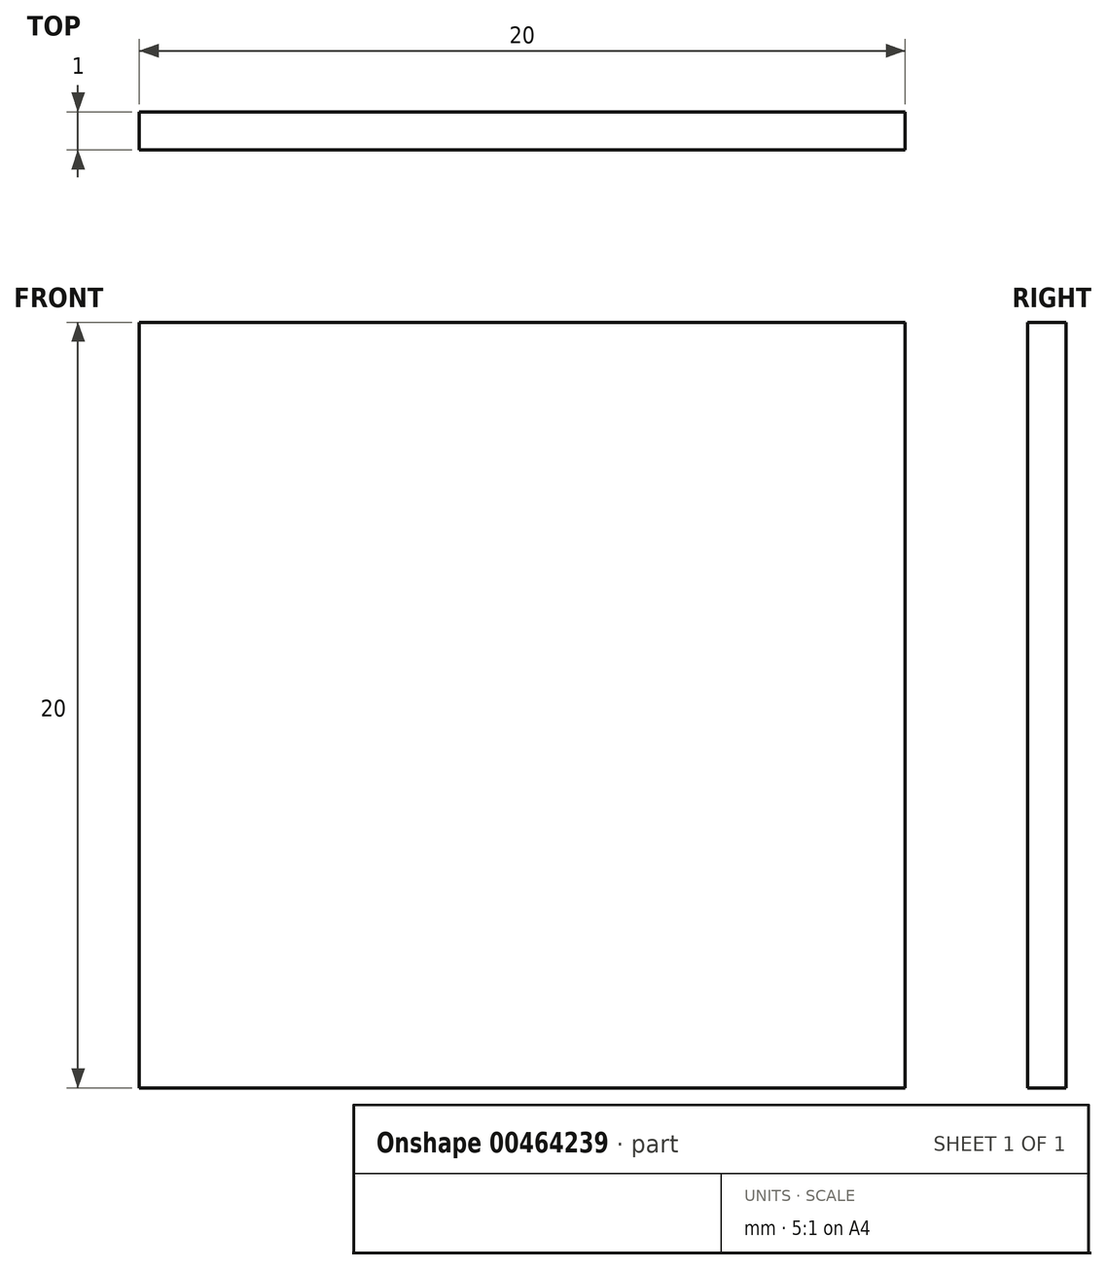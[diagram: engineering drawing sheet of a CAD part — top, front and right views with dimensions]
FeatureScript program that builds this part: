
annotation { "Feature Type Name" : "Feature", "Feature Type Description" : "" }
export const myFeature = defineFeature(function(context is Context, id is Id, definition is map)
    precondition{}
    {
        {
            var Q0;
            Q0=qCreatedBy(makeId("Front.planeOp"),FACE);
            var sketch = newSketch(context, id + "F0", { "sketchPlane" : qUnion([Q0])});
            skLineSegment(sketch, "E0.bottom", {"start": v(0, 0) * mm, "end": v(20, 0) * mm});
            skLineSegment(sketch, "E0.top", {"start": v(0, 20) * mm, "end": v(20, 20) * mm});
            skLineSegment(sketch, "E0.left", {"start": v(0, 0) * mm, "end": v(0, 20) * mm});
            skLineSegment(sketch, "E0.right", {"start": v(20, 0) * mm, "end": v(20, 20) * mm});
            skSolve(sketch);
        }
        {
            var Q0;
            Q0 = qSketchRegion(id + "F0", true);
            extrude(context, id + "F1", {"entities" : qUnion([Q0]), "depth" : 1 * mm});
        }
    });
